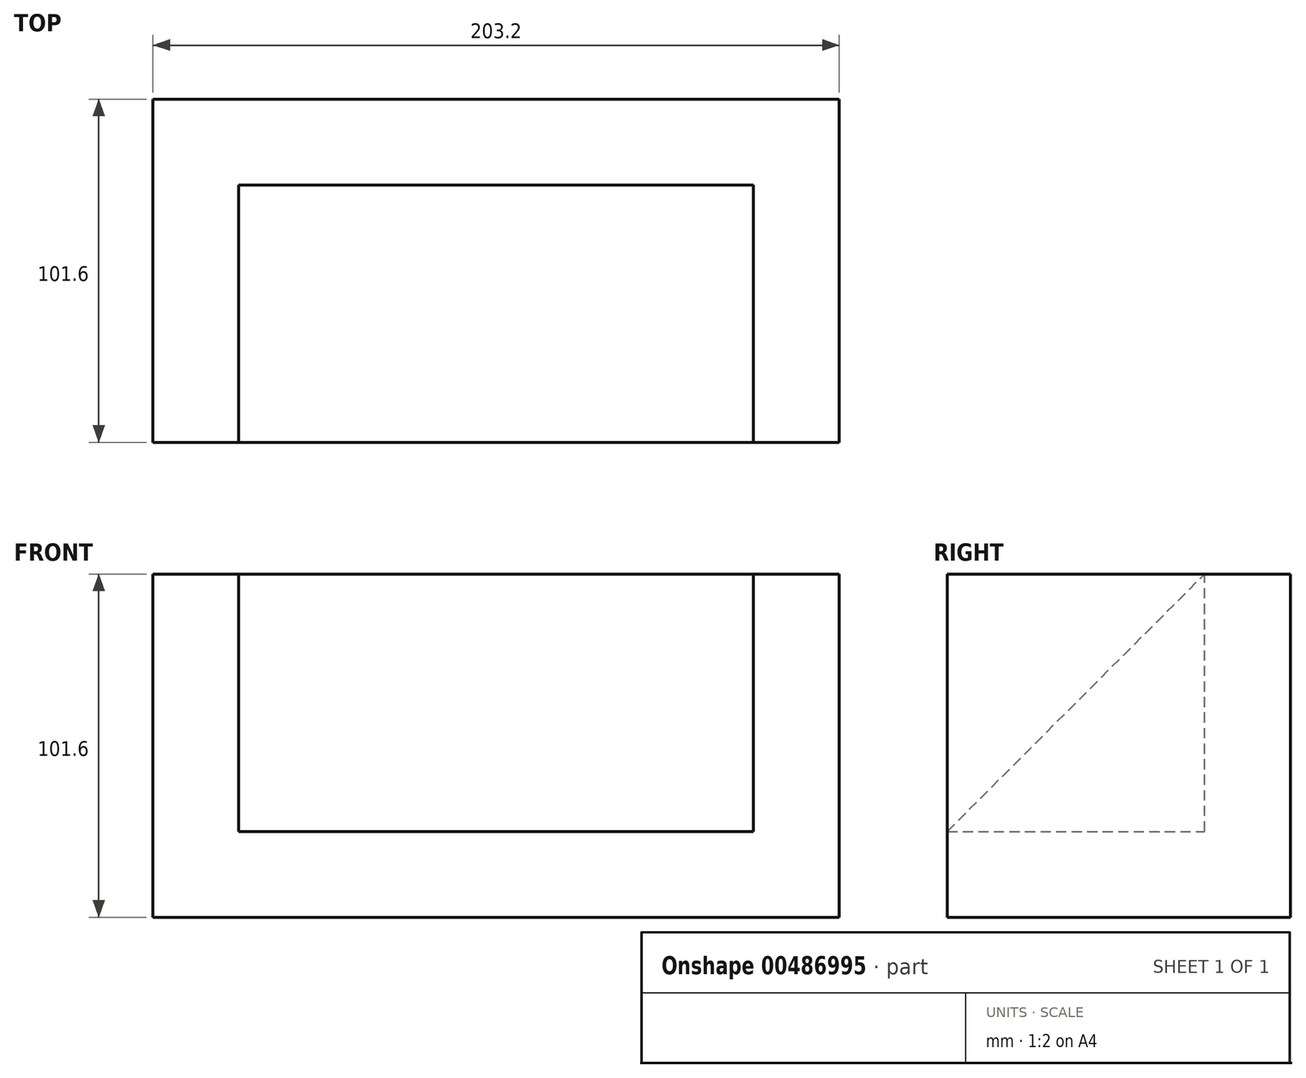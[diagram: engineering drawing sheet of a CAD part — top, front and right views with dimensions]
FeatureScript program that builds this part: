
annotation { "Feature Type Name" : "Feature", "Feature Type Description" : "" }
export const myFeature = defineFeature(function(context is Context, id is Id, definition is map)
    precondition{}
    {
        {
            var Q0;
            Q0=qCreatedBy(makeId("Front.planeOp"),FACE);
            var sketch = newSketch(context, id + "F0", { "sketchPlane" : qUnion([Q0])});
            skLineSegment(sketch, "E0.bottom", {"start": v(0, 0) * mm, "end": v(25.4, 0) * mm});
            skLineSegment(sketch, "E0.top", {"start": v(0, 101.6) * mm, "end": v(25.4, 101.6) * mm});
            skLineSegment(sketch, "E0.left", {"start": v(0, 25.4) * mm, "end": v(0, 101.6) * mm});
            skLineSegment(sketch, "E0.right", {"start": v(25.4, 0) * mm, "end": v(25.4, 101.6) * mm});
            skLineSegment(sketch, "E1.bottom", {"start": v(0, 0) * mm, "end": v(-152.4, 0) * mm});
            skLineSegment(sketch, "E1.top", {"start": v(0, 25.4) * mm, "end": v(-152.4, 25.4) * mm});
            skLineSegment(sketch, "E2.bottom", {"start": v(-152.4, 0) * mm, "end": v(-177.8, 0) * mm});
            skLineSegment(sketch, "E2.top", {"start": v(-152.4, 101.6) * mm, "end": v(-177.8, 101.6) * mm});
            skLineSegment(sketch, "E2.left", {"start": v(-152.4, 25.4) * mm, "end": v(-152.4, 101.6) * mm});
            skLineSegment(sketch, "E2.right", {"start": v(-177.8, 0) * mm, "end": v(-177.8, 101.6) * mm});
            skLineSegment(sketch, "E3.bottom", {"start": v(-152.4, 101.6) * mm, "end": v(0, 101.6) * mm});
            skLineSegment(sketch, "E3.top", {"start": v(-152.4, 25.4) * mm, "end": v(0, 25.4) * mm});
            skLineSegment(sketch, "E3.left", {"start": v(-152.4, 101.6) * mm, "end": v(-152.4, 25.4) * mm});
            skLineSegment(sketch, "E3.right", {"start": v(0, 101.6) * mm, "end": v(0, 25.4) * mm});
            skSolve(sketch);
        }
        {
            var Q0;
            Q0=makeQuery(id+"F0.imprint","IMPRINT",FACE,{"disambiguationData":[TD([[makeQuery(id+"F0.imprint","IMPRINT",EDGE,{"derivedFrom":sQuery(id+"F0.wireOp",EDGE,"E0.bottom")}),1.0]])]});
            extrude(context, id + "F1", {"entities" : qUnion([Q0]), "depth" : 101.6 * mm});
        }
        {
            var Q0;
            Q0=makeQuery(id+"F0.imprint","IMPRINT",FACE,{"disambiguationData":[TD([[makeQuery(id+"F0.imprint","IMPRINT",EDGE,{"derivedFrom":sQuery(id+"F0.wireOp",EDGE,"E3.bottom")}),-1.0]])]});
            extrude(context, id + "F2", {"entities" : qUnion([Q0]), "operationType" : NewBodyOperationType.ADD, "depth" : 25.4 * mm});
        }
        {
            var Q0;
            Q0=makeQuery(id+"F2.opExtrude","CAP_FACE",FACE,{"disambiguationData":[OSD([sQuery(id+"F0.wireOp",EDGE,"E3.bottom"),sQuery(id+"F0.wireOp",EDGE,"E3.top"),sQuery(id+"F0.wireOp",EDGE,"E3.left"),sQuery(id+"F0.wireOp",EDGE,"E3.right")])],"isStart":false});
            extrude(context, id + "F3", {"entities" : qUnion([Q0]), "depth" : 76.2 * mm});
        }
        {
            var Q0;
            Q0=makeQuery(id+"F3.opExtrude","CAP_EDGE",EDGE,{"disambiguationData":[OSD([sQuery(id+"F0.wireOp",EDGE,"E3.bottom")])],"isStart":false});
            chamfer(context, id + "F4", {"entities" : qUnion([Q0]), "width" : 76.2 * mm, "tangentPropagation" : true});
        }
    });
